# Revit family: 302991001_Sanitario Avanti Plus Blanco
name_source: partatom
category: Plumbing Fixtures
units: mm (PartAtom-declared; Revit-internal decimal feet)

## family parameters
Always vertical = Yes
Cut with Voids When Loaded = No
Host = Floor
OmniClass Number = 23.31.19.17
OmniClass Title = Toilets With Tank
Part Type = Normal
Room Calculation Point = No
Round Connector Dimension = Use Diameter
Shared = No

## types (1)
- 302991001_Sanitario Avanti Plus Blanco
    Acabado = Brillante
    Alto = 70 cm
    Altura de la taza = 37 cm
    Ancho = 43 cm
    Capacidad de descarga = 300 g
    Colección = 200704
    Consumo de agua = 4.8 lt
    Creado por = IDD
    Description = Adquiere ahora este sanitario con taza y tanque separados, ideal para reemplazar por separado.
    Espejo de agua = 19 x 22.2 cm
    Fecha de creación = 30/07/2020
    Garantía = Garantia completa para siempre en la porcelana
    Garantías de otros componentes = 5 años en grifería tanque y asiento.
    Incluye = Taza y tanque, tapa tanque, botón de descarga tipo push, asiento sanitario cierre suave
    Largo = 67 cm
    Línea = Avanti Alongado
    Material = Corona_Porcelana_Sanitaria
    Materiales = Porcelana sanitaria
    Resistencia = Sanitario con menor probabilidad de fugas y mayor resistencia a ataques químicos
    Sistema de descarga = Botón tipo push
    Tipo de asiento = Cierre lento
    Tipo de instalación = A piso
    Tipo de sifón = Oculto
    Tipo de tanque = Taza y tanque
    Tipo de válvula = Válvula de descarga sencilla
    URL = https://www.corona.co
    Uso = Residencial

## geometry (parser evidence)
native form markers: Sweep x10
no freeform markers — native parametric forms only
